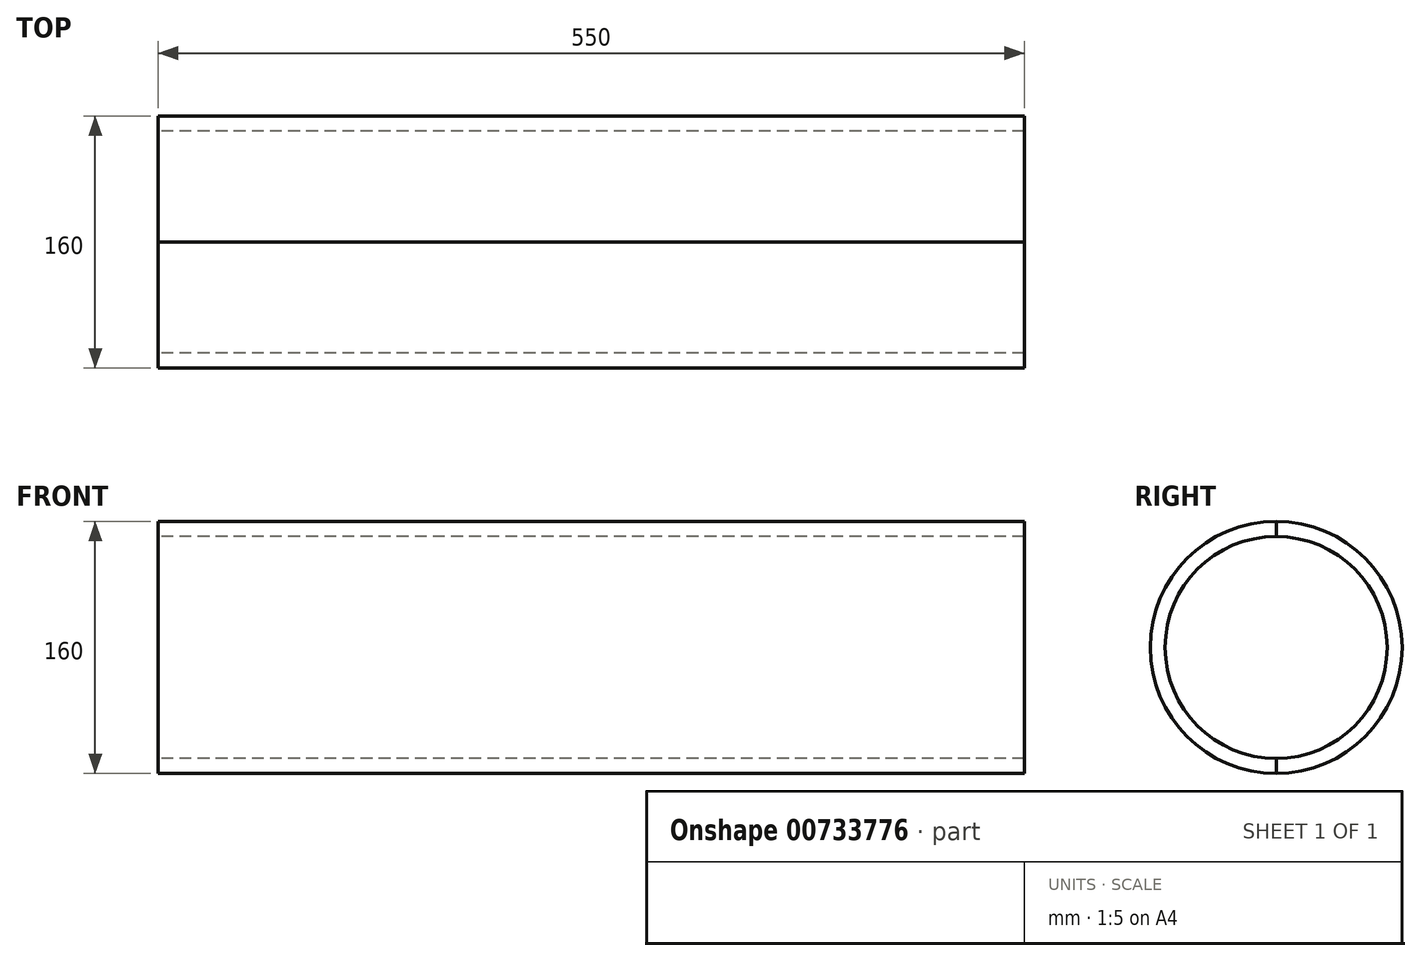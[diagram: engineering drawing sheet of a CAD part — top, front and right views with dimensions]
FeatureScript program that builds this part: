
annotation { "Feature Type Name" : "Feature", "Feature Type Description" : "" }
export const myFeature = defineFeature(function(context is Context, id is Id, definition is map)
    precondition{}
    {
        {
            var Q0;
            Q0=qCreatedBy(makeId("Front.planeOp"),FACE);
            var sketch = newSketch(context, id + "F0", { "sketchPlane" : qUnion([Q0])});
            skPoint(sketch, "E0.middle", {"position": v(0, 1.97) * mm});
            skLineSegment(sketch, "E1.bottom", {"start": v(275, -80) * mm, "end": v(-275, -80) * mm});
            skLineSegment(sketch, "E1.top", {"start": v(275, 80) * mm, "end": v(-275, 80) * mm});
            skPoint(sketch, "E1.middle", {"position": v(0, 0) * mm});
            skLineSegment(sketch, "E2", {"start": v(164.04, 0) * mm, "end": v(275, 0) * mm});
            skLineSegment(sketch, "E3.bottom", {"start": v(275, -70.5) * mm, "end": v(-275, -70.5) * mm});
            skLineSegment(sketch, "E3.top", {"start": v(275, 70.5) * mm, "end": v(-275, 70.5) * mm});
            skLineSegment(sketch, "E3.left", {"start": v(275, -70.5) * mm, "end": v(275, 70.5) * mm});
            skLineSegment(sketch, "E3.right", {"start": v(-275, -70.5) * mm, "end": v(-275, 70.5) * mm});
            skLineSegment(sketch, "E4", {"start": v(-275, 70.5) * mm, "end": v(-275, 80) * mm});
            skLineSegment(sketch, "E5", {"start": v(275, 70.5) * mm, "end": v(275, 80) * mm});
            skPoint(sketch, "E6.orphan", {"position": v(-1.73, 80) * mm});
            skLineSegment(sketch, "E7", {"start": v(275, -70.5) * mm, "end": v(275, -80) * mm});
            skLineSegment(sketch, "E8", {"start": v(-275, -70.5) * mm, "end": v(-275, -80) * mm});
            skPoint(sketch, "E9.orphan", {"position": v(1.73, -80) * mm});
            skSolve(sketch);
        }
        {
            var Q0;
            Q0=makeQuery(id+"F0.imprint","IMPRINT",FACE,{"disambiguationData":[TD([[makeQuery(id+"F0.imprint","IMPRINT",EDGE,{"derivedFrom":sQuery(id+"F0.wireOp",EDGE,"E1.top")}),1.0]])]});
            var Q1;
            Q1=makeQuery(id+"F0.imprint","IMPRINT",FACE,{"disambiguationData":[TD([[makeQuery(id+"F0.imprint","IMPRINT",EDGE,{"derivedFrom":sQuery(id+"F0.wireOp",EDGE,"E1.bottom")}),-1.0]])]});
            var Q2;
            Q2=sQuery(id+"F0.wireOp",EDGE,"E2");
            revolve(context, id + "F1", {"entities" : qUnion([Q0, Q1]), "axis" : qUnion([Q2]), "revolveType" : RevolveType.ONE_DIRECTION, "angle" : 180 * degree});
        }
        {
            var Q0;
            Q0=makeQuery(id+"F1.opRevolve","SWEPT_BODY",BODY,{"disambiguationData":[OSD([sQuery(id+"F0.wireOp",EDGE,"E1.top"),sQuery(id+"F0.wireOp",EDGE,"E3.top"),sQuery(id+"F0.wireOp",EDGE,"E4"),sQuery(id+"F0.wireOp",EDGE,"E5")])]});
            transform(context, id + "F2", {"entities" : qUnion([Q0]), "transformType" : TransformType.TRANSLATION_3D, "dx" : 0 * mm, "dy" : 0 * mm, "dz" : 0 * mm, "makeCopy" : true});
        }
    });
